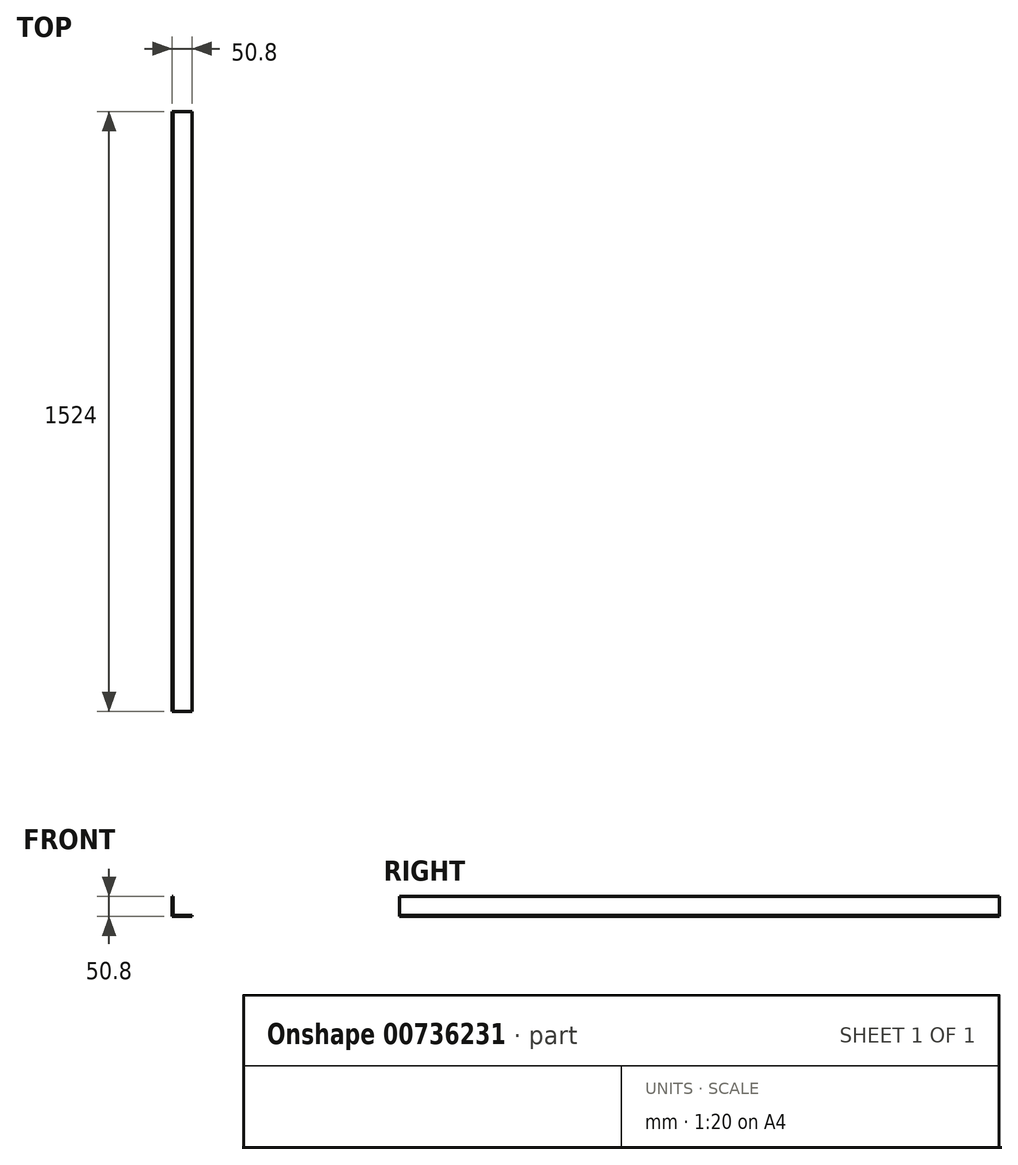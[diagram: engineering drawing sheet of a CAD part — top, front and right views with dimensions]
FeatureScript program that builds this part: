
annotation { "Feature Type Name" : "Feature", "Feature Type Description" : "" }
export const myFeature = defineFeature(function(context is Context, id is Id, definition is map)
    precondition{}
    {
        {
            var Q0;
            Q0=qCreatedBy(makeId("Front.planeOp"),FACE);
            var sketch = newSketch(context, id + "F0", { "sketchPlane" : qUnion([Q0])});
            skLineSegment(sketch, "E0.bottom", {"start": v(0, 0) * mm, "end": v(50.8, 0) * mm});
            skLineSegment(sketch, "E0.top", {"start": v(0, 3.18) * mm, "end": v(50.8, 3.18) * mm});
            skLineSegment(sketch, "E0.left", {"start": v(0, 0) * mm, "end": v(0, 3.18) * mm});
            skLineSegment(sketch, "E0.right", {"start": v(50.8, 0) * mm, "end": v(50.8, 3.18) * mm});
            skLineSegment(sketch, "E1.bottom", {"start": v(0, 0) * mm, "end": v(3.18, 0) * mm});
            skLineSegment(sketch, "E1.top", {"start": v(0, 50.8) * mm, "end": v(3.17, 50.8) * mm});
            skLineSegment(sketch, "E1.left", {"start": v(0, 0) * mm, "end": v(0, 50.8) * mm});
            skLineSegment(sketch, "E1.right", {"start": v(3.18, 0) * mm, "end": v(3.17, 50.8) * mm});
            skSolve(sketch);
        }
        {
            var Q0;
            Q0 = qSketchRegion(id + "F0", true);
            extrude(context, id + "F1", {"entities" : qUnion([Q0]), "oppositeDirection" : true, "depth" : 1524 * mm, "offsetDistance" : 25.4 * mm});
        }
    });
